# Revit family: EuroTambours_Double
name_source: partatom
category: Furniture
revit_build: Autodesk Revit 2016 (Build: 20150714_1515(x64)
units: mm (PartAtom-declared; Revit-internal decimal feet)

## family parameters
Always vertical = Yes
Cut with Voids When Loaded = No
OmniClass Number = 23.40.20.00
OmniClass Title = General Furniture and Specialties
Room Calculation Point = No
Shared = No
Work Plane-Based = No

## types (14) — shared parameters
Depth = 430 mm

## per-type parameters (varying)
| type | Doors height | Height | Plinth height | Start door height | Tambour array | Width |
| ET410/TB | 356 mm | 495 mm  [stored 1.62402 ft] | 55 mm  [stored 0.180446 ft] | -35 mm  [stored -0.114829 ft] | 15 | 1000 mm  [stored 3.28084 ft] |
| ET410/06 | 556 mm | 695 mm  [stored 2.28018 ft] | 85 mm  [stored 0.278871 ft] | -5 mm  [stored -0.0164042 ft] | 15 | 1000 mm  [stored 3.28084 ft] |
| ET410/10 | 891 mm | 1030 mm  [stored 3.37927 ft] | 85 mm  [stored 0.278871 ft] | -5 mm  [stored -0.0164042 ft] | 15 | 1000 mm  [stored 3.28084 ft] |
| ET410/11 | 1042 mm | 1181 mm  [stored 3.87467 ft] | 85 mm  [stored 0.278871 ft] | -5 mm  [stored -0.0164042 ft] | 15 | 1000 mm  [stored 3.28084 ft] |
| ET410/13 | 1191 mm  [stored 3.90748 ft] | 1330 mm  [stored 4.36352 ft] | 85 mm  [stored 0.278871 ft] | -5 mm  [stored -0.0164042 ft] | 15 | 1000 mm  [stored 3.28084 ft] |
| ET410/17 | 1498 mm  [stored 4.9147 ft] | 1637 mm  [stored 5.37073 ft] | 85 mm  [stored 0.278871 ft] | -5 mm  [stored -0.0164042 ft] | 15 | 1000 mm  [stored 3.28084 ft] |
| ET410/19 | 1841 mm  [stored 6.04003 ft] | 1980 mm  [stored 6.49606 ft] | 85 mm  [stored 0.278871 ft] | -5 mm  [stored -0.0164042 ft] | 15 | 1000 mm  [stored 3.28084 ft] |
| ET412/TB | 356 mm | 495 mm  [stored 1.62402 ft] | 55 mm  [stored 0.180446 ft] | -35 mm  [stored -0.114829 ft] | 18 | 1200 mm |
| ET412/06 | 556 mm | 695 mm  [stored 2.28018 ft] | 85 mm  [stored 0.278871 ft] | -5 mm  [stored -0.0164042 ft] | 18 | 1200 mm |
| ET412/10 | 891 mm | 1030 mm  [stored 3.37927 ft] | 85 mm  [stored 0.278871 ft] | -5 mm  [stored -0.0164042 ft] | 18 | 1200 mm |
| ET412/11 | 1042 mm | 1181 mm  [stored 3.87467 ft] | 85 mm  [stored 0.278871 ft] | -5 mm  [stored -0.0164042 ft] | 18 | 1200 mm |
| ET412/13 | 1191 mm  [stored 3.90748 ft] | 1330 mm  [stored 4.36352 ft] | 85 mm  [stored 0.278871 ft] | -5 mm  [stored -0.0164042 ft] | 18 | 1200 mm |
| ET412/17 | 1498 mm  [stored 4.9147 ft] | 1637 mm  [stored 5.37073 ft] | 85 mm  [stored 0.278871 ft] | -5 mm  [stored -0.0164042 ft] | 18 | 1200 mm |
| ET412/19 | 1841 mm  [stored 6.04003 ft] | 1980 mm  [stored 6.49606 ft] | 85 mm  [stored 0.278871 ft] | -5 mm  [stored -0.0164042 ft] | 18 | 1200 mm |

note: [stored X ft] marks values corroborated as IEEE doubles in the binary element streams (Revit-internal decimal feet)

## geometry (parser evidence)
native form markers: Sweep x2
no freeform markers — native parametric forms only
